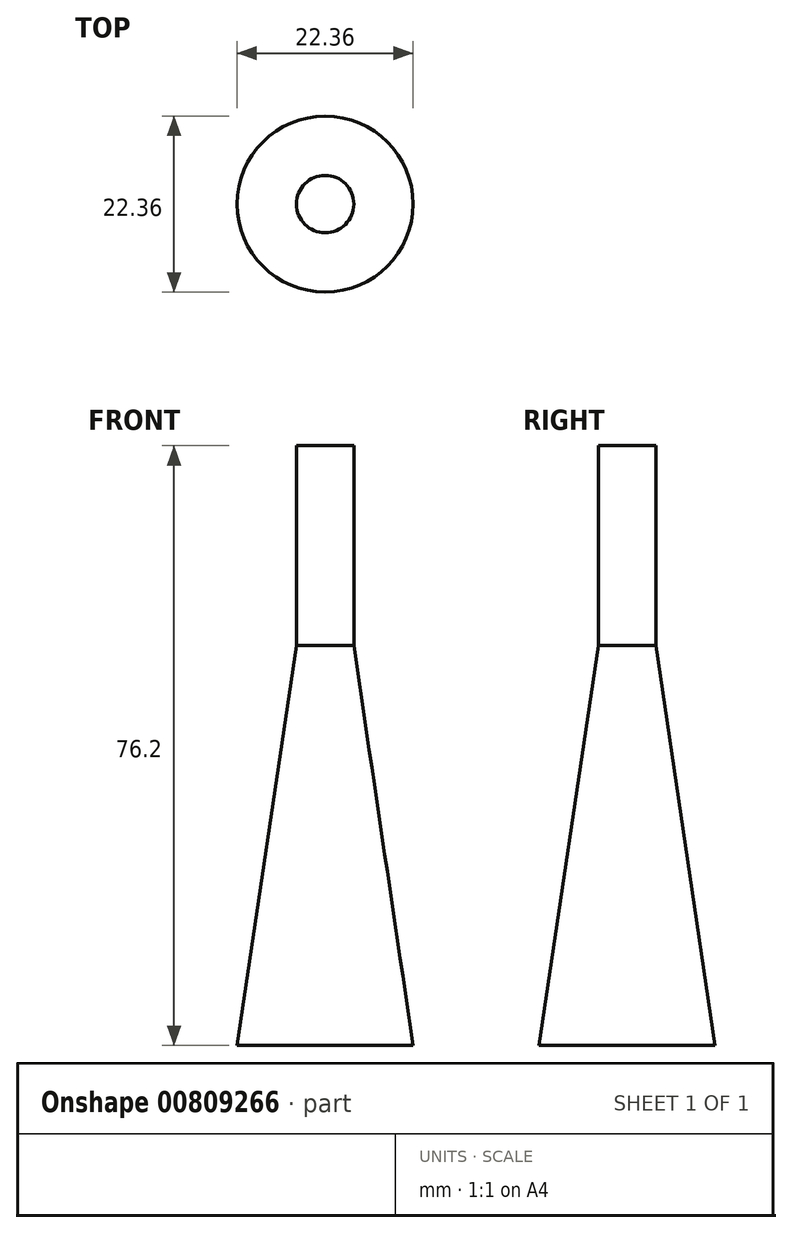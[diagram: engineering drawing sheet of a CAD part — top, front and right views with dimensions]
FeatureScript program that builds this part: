
annotation { "Feature Type Name" : "Feature", "Feature Type Description" : "" }
export const myFeature = defineFeature(function(context is Context, id is Id, definition is map)
    precondition{}
    {
        {
            var Q0;
            Q0=qCreatedBy(makeId("Front.planeOp"),FACE);
            var sketch = newSketch(context, id + "F0", { "sketchPlane" : qUnion([Q0])});
            skLineSegment(sketch, "E0", {"start": v(0, 109.96) * mm, "end": v(0, -45.1) * mm, "construction": true});
            skLineSegment(sketch, "E1", {"start": v(0, 0) * mm, "end": v(11.18, 0) * mm});
            skLineSegment(sketch, "E2", {"start": v(11.18, 0) * mm, "end": v(0, 75.38) * mm});
            skLineSegment(sketch, "E3", {"start": v(0, 75.38) * mm, "end": v(0, 0) * mm});
            skSolve(sketch);
        }
        {
            var Q0;
            Q0=makeQuery(id+"F0.imprint","IMPRINT",FACE,{"disambiguationData":[TD([[makeQuery(id+"F0.imprint","IMPRINT",EDGE,{"derivedFrom":sQuery(id+"F0.wireOp",EDGE,"E1")}),1.0]])]});
            var Q1;
            Q1=sQuery(id+"F0.wireOp",EDGE,"E0");
            revolve(context, id + "F1", {"surfaceOperationType" : NewSurfaceOperationType.NEW, "entities" : qUnion([Q0]), "axis" : qUnion([Q1]), "revolveType" : RevolveType.FULL});
        }
        {
            var Q0;
            Q0=qCreatedBy(makeId("Right.planeOp"),FACE);
            var sketch = newSketch(context, id + "F2", { "sketchPlane" : qUnion([Q0])});
            skLineSegment(sketch, "E4.bottom", {"start": v(24.88, 76.2) * mm, "end": v(-31.42, 76.2) * mm});
            skLineSegment(sketch, "E4.top", {"start": v(24.88, 50.8) * mm, "end": v(-31.42, 50.8) * mm});
            skLineSegment(sketch, "E4.left", {"start": v(24.88, 76.2) * mm, "end": v(24.88, 50.8) * mm});
            skLineSegment(sketch, "E4.right", {"start": v(-31.42, 76.2) * mm, "end": v(-31.42, 50.8) * mm});
            skSolve(sketch);
        }
        {
            var Q0;
            Q0 = qSketchRegion(id + "F2", true);
            extrude(context, id + "F3", {"entities" : qUnion([Q0]), "operationType" : NewBodyOperationType.REMOVE, "endBound" : BoundingType.SYMMETRIC, "oppositeDirection" : true, "depth" : 20.32 * mm, "offsetDistance" : 25.4 * mm});
        }
        {
            var Q0;
            Q0=makeQuery(id+"F3.boolean.opBoolean","COPY",FACE,{"derivedFrom":makeQuery(id+"F3.opExtrude","SWEPT_FACE",FACE,{"disambiguationData":[OSD([sQuery(id+"F2.wireOp",EDGE,"E4.top")])]})});
            extrude(context, id + "F4", {"entities" : qUnion([Q0]), "operationType" : NewBodyOperationType.ADD, "depth" : 25.4 * mm, "offsetDistance" : 25.4 * mm});
        }
    });
